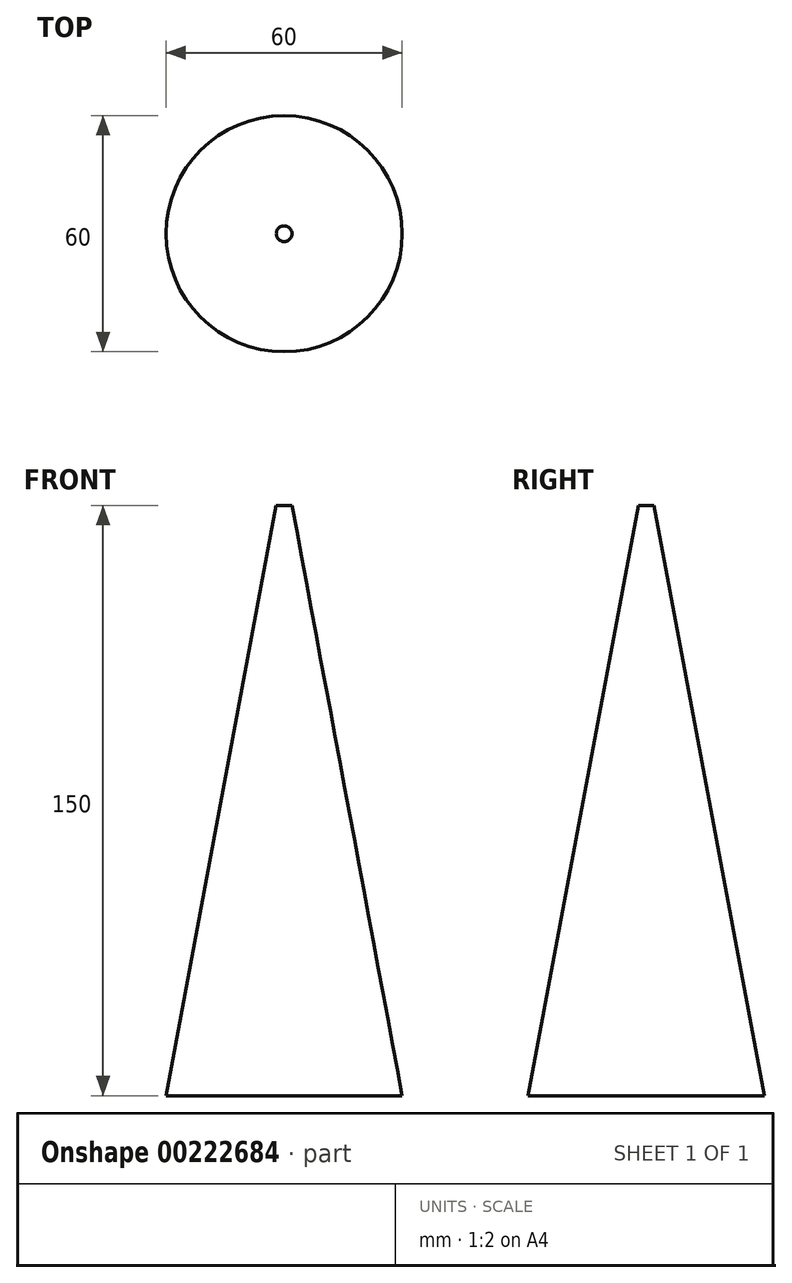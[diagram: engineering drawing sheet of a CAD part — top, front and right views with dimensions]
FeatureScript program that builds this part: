
annotation { "Feature Type Name" : "Feature", "Feature Type Description" : "" }
export const myFeature = defineFeature(function(context is Context, id is Id, definition is map)
    precondition{}
    {
        {
            var Q0;
            Q0=qCreatedBy(makeId("Front.planeOp"),FACE);
            var sketch = newSketch(context, id + "F0", { "sketchPlane" : qUnion([Q0])});
            skLineSegment(sketch, "E0", {"start": v(0, 0) * mm, "end": v(30, 0) * mm});
            skLineSegment(sketch, "E1", {"start": v(0, 150) * mm, "end": v(0, 0) * mm});
            skLineSegment(sketch, "E2", {"start": v(0, 150) * mm, "end": v(2, 150) * mm});
            skLineSegment(sketch, "E3", {"start": v(30, 0) * mm, "end": v(2, 150) * mm});
            skSolve(sketch);
        }
        {
            var Q0;
            Q0=makeQuery(id+"F0.imprint","IMPRINT",FACE,{"disambiguationData":[TD([[makeQuery(id+"F0.imprint","IMPRINT",EDGE,{"derivedFrom":sQuery(id+"F0.wireOp",EDGE,"E0")}),1.0]])]});
            var Q1;
            Q1=sQuery(id+"F0.wireOp",EDGE,"E1");
            revolve(context, id + "F1", {"entities" : qUnion([Q0]), "axis" : qUnion([Q1]), "revolveType" : RevolveType.FULL});
        }
    });
